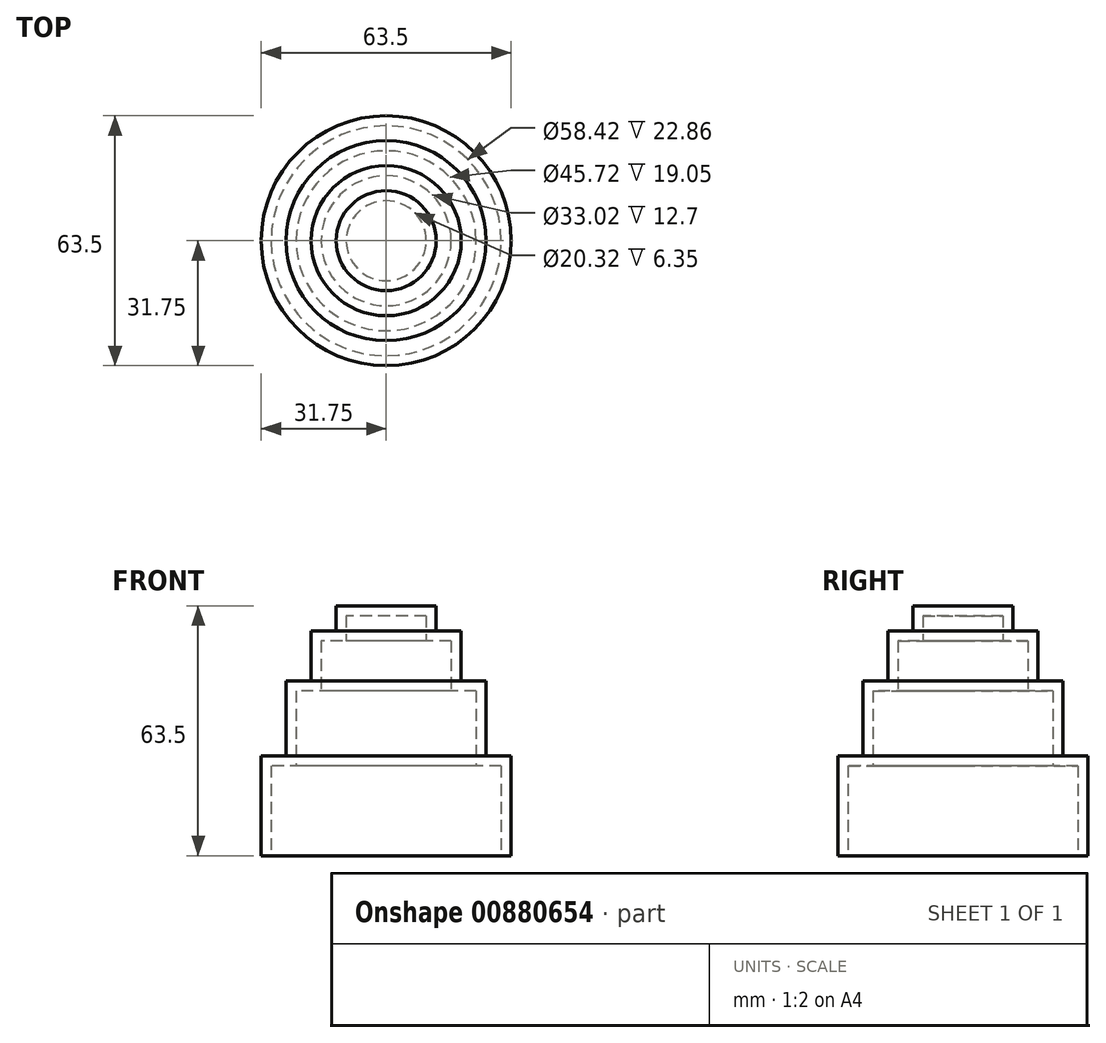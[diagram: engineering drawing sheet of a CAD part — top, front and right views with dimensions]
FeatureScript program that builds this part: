
annotation { "Feature Type Name" : "Feature", "Feature Type Description" : "" }
export const myFeature = defineFeature(function(context is Context, id is Id, definition is map)
    precondition{}
    {
        {
            var Q0;
            Q0=qCreatedBy(makeId("Top.planeOp"),FACE);
            var sketch = newSketch(context, id + "F0", { "sketchPlane" : qUnion([Q0])});
            skCircle(sketch, "E0", {"center": v(0, 0) * mm, "radius": 31.75 * mm});
            skSolve(sketch);
        }
        {
            var Q0;
            Q0 = qSketchRegion(id + "F0", true);
            extrude(context, id + "F1", {"entities" : qUnion([Q0]), "depth" : 25.4 * mm, "offsetDistance" : 25.4 * mm});
        }
        {
            var Q0;
            Q0=makeQuery(id+"F1.opExtrude","CAP_FACE",FACE,{"disambiguationData":[OSD([sQuery(id+"F0.wireOp",EDGE,"E0")])],"isStart":false});
            var sketch = newSketch(context, id + "F2", { "sketchPlane" : qUnion([Q0])});
            skCircle(sketch, "E1", {"center": v(0, 0) * mm, "radius": 25.4 * mm});
            skSolve(sketch);
        }
        {
            var Q0;
            Q0 = qSketchRegion(id + "F2", true);
            extrude(context, id + "F3", {"entities" : qUnion([Q0]), "operationType" : NewBodyOperationType.ADD, "depth" : 19.05 * mm, "offsetDistance" : 25.4 * mm});
        }
        {
            var Q0;
            Q0=makeQuery(id+"F3.opExtrude","CAP_FACE",FACE,{"disambiguationData":[OSD([sQuery(id+"F2.wireOp",EDGE,"E1")])],"isStart":false});
            var sketch = newSketch(context, id + "F4", { "sketchPlane" : qUnion([Q0])});
            skCircle(sketch, "E2", {"center": v(0, 0) * mm, "radius": 19.05 * mm});
            skSolve(sketch);
        }
        {
            var Q0;
            Q0 = qSketchRegion(id + "F4", true);
            extrude(context, id + "F5", {"entities" : qUnion([Q0]), "operationType" : NewBodyOperationType.ADD, "depth" : 12.7 * mm, "offsetDistance" : 25.4 * mm});
        }
        {
            var Q0;
            Q0=makeQuery(id+"F5.opExtrude","CAP_FACE",FACE,{"disambiguationData":[OSD([sQuery(id+"F4.wireOp",EDGE,"E2")])],"isStart":false});
            var sketch = newSketch(context, id + "F6", { "sketchPlane" : qUnion([Q0])});
            skCircle(sketch, "E3", {"center": v(0, 0) * mm, "radius": 12.7 * mm});
            skSolve(sketch);
        }
        {
            var Q0;
            Q0 = qSketchRegion(id + "F6", true);
            extrude(context, id + "F7", {"entities" : qUnion([Q0]), "operationType" : NewBodyOperationType.ADD, "depth" : 6.35 * mm, "offsetDistance" : 25.4 * mm});
        }
        {
            var Q0;
            Q0=makeQuery(id+"F1.opExtrude","CAP_FACE",FACE,{"disambiguationData":[OSD([sQuery(id+"F0.wireOp",EDGE,"E0")])],"isStart":true});
            shell(context, id + "F8", {"entities" : qUnion([Q0]), "thickness" : 2.54 * mm});
        }
    });
